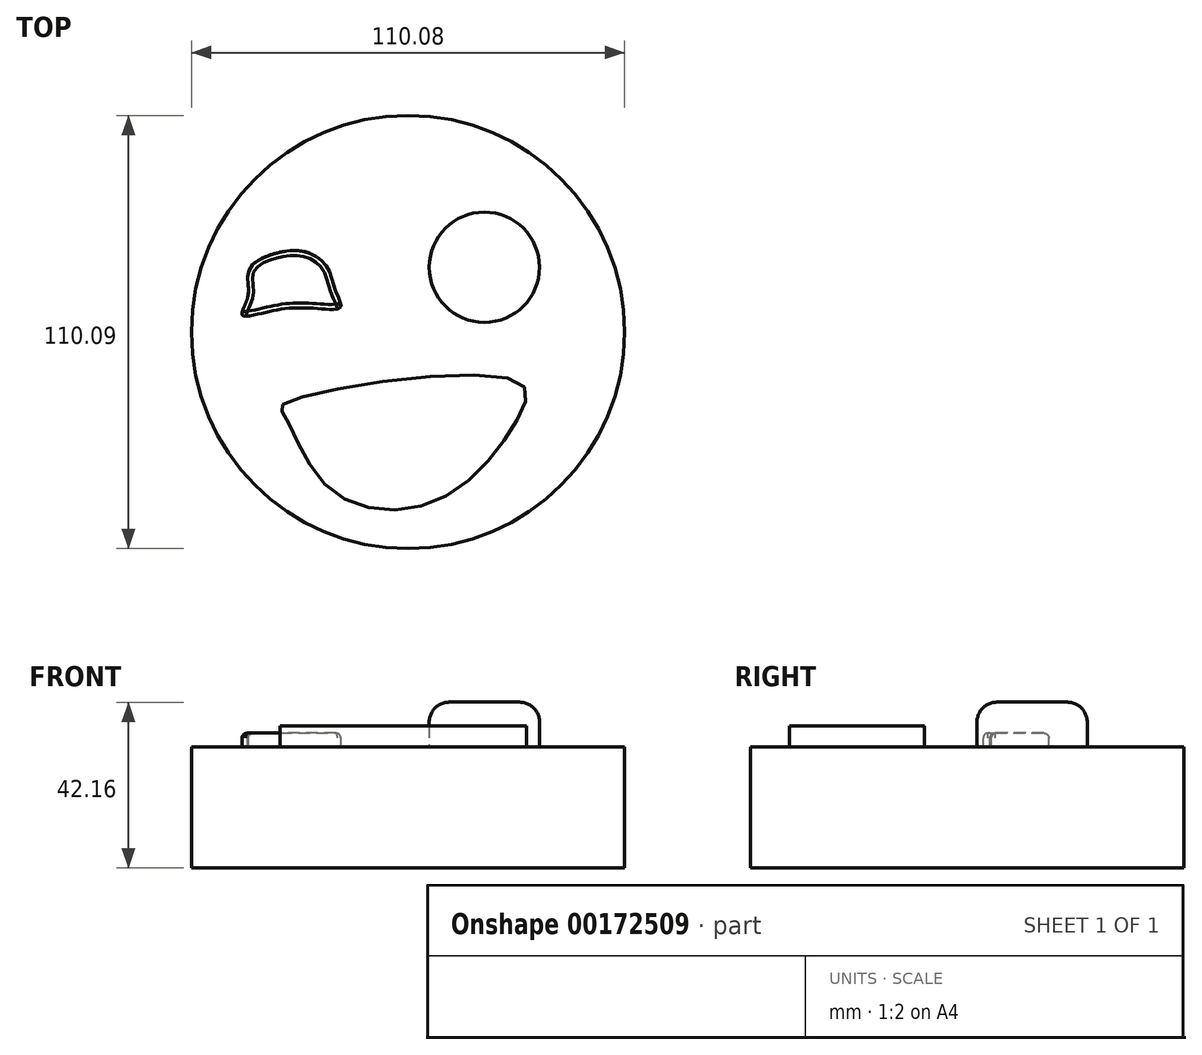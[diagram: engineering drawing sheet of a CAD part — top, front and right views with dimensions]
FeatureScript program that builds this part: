
annotation { "Feature Type Name" : "Feature", "Feature Type Description" : "" }
export const myFeature = defineFeature(function(context is Context, id is Id, definition is map)
    precondition{}
    {
        {
            var Q0;
            Q0=qCreatedBy(makeId("Top.planeOp"),FACE);
            var sketch = newSketch(context, id + "F0", { "sketchPlane" : qUnion([Q0])});
            skCircle(sketch, "E0", {"center": v(0.2, -0.69) * mm, "radius": 55.04 * mm});
            skSolve(sketch);
        }
        {
            var Q0;
            Q0=makeQuery(id+"F0.imprint","IMPRINT",FACE,{"disambiguationData":[TD([[makeQuery(id+"F0.imprint","IMPRINT",EDGE,{"derivedFrom":sQuery(id+"F0.wireOp",EDGE,"E0")}),1.0]])]});
            extrude(context, id + "F1", {"entities" : qUnion([Q0]), "depth" : 30.73 * mm});
        }
        {
            var Q0;
            Q0=makeQuery(id+"F1.opExtrude","CAP_FACE",FACE,{"disambiguationData":[OSD([sQuery(id+"F0.wireOp",EDGE,"E0")])],"isStart":false});
            var sketch = newSketch(context, id + "F2", { "sketchPlane" : qUnion([Q0])});
            skCircle(sketch, "E1", {"center": v(19.59, 15.77) * mm, "radius": 14 * mm});
            skSolve(sketch);
        }
        {
            var Q0;
            Q0=makeQuery(id+"F2.imprint","IMPRINT",FACE,{"disambiguationData":[TD([[makeQuery(id+"F2.imprint","IMPRINT",EDGE,{"derivedFrom":sQuery(id+"F2.wireOp",EDGE,"E1")}),-1.0]])]});
            var sketch = newSketch(context, id + "F3", { "sketchPlane" : qUnion([Q0])});
            skFitSpline(sketch, "E2", {"points": [v(-40.54, 8.13) * mm, v(-40.54, 13.22) * mm, v(-39.17, 16.55) * mm, v(-33.5, 19.3) * mm, v(-25.85, 19.68) * mm, v(-20.37, 15.77) * mm, v(-18.22, 9.7) * mm, v(-17.04, 5.58) * mm, v(-29.77, 5.39) * mm, v(-41.91, 3.62) * mm, v(-40.54, 8.13) * mm]});
            skSolve(sketch);
        }
        {
            var Q0;
            Q0=makeQuery(id+"F2.imprint","IMPRINT",FACE,{"disambiguationData":[TD([[makeQuery(id+"F2.imprint","IMPRINT",EDGE,{"derivedFrom":sQuery(id+"F2.wireOp",EDGE,"E1")}),1.0]])]});
            extrude(context, id + "F4", {"entities" : qUnion([Q0]), "operationType" : NewBodyOperationType.ADD, "depth" : 6.1 * mm});
        }
        {
            var Q0;
            Q0=makeQuery(id+"F3.imprint","IMPRINT",FACE,{"disambiguationData":[TD([[makeQuery(id+"F3.imprint","IMPRINT",EDGE,{"derivedFrom":sQuery(id+"F3.wireOp",EDGE,"E2")}),-1.0]])]});
            extrude(context, id + "F5", {"entities" : qUnion([Q0]), "operationType" : NewBodyOperationType.ADD, "depth" : 3.56 * mm});
        }
        {
            var Q0;
            Q0=makeQuery(id+"F1.opExtrude","CAP_FACE",FACE,{"disambiguationData":[OSD([sQuery(id+"F0.wireOp",EDGE,"E0")])],"isStart":false});
            var sketch = newSketch(context, id + "F6", { "sketchPlane" : qUnion([Q0])});
            skFitSpline(sketch, "E3", {"points": [v(-31.73, -19.1) * mm, v(-31.14, -22.03) * mm, v(-19.78, -40.45) * mm, v(7.25, -43.58) * mm, v(28, -22.82) * mm, v(27.62, -13.02) * mm, v(-31.73, -19.1) * mm]});
            skSolve(sketch);
        }
        {
            var Q0;
            Q0=makeQuery(id+"F6.imprint","IMPRINT",FACE,{"disambiguationData":[TD([[makeQuery(id+"F6.imprint","IMPRINT",EDGE,{"derivedFrom":sQuery(id+"F6.wireOp",EDGE,"E3")}),1.0]])]});
            var Q1;
            Q1=makeQuery(id+"F4.opExtrude","CAP_FACE",FACE,{"disambiguationData":[OSD([sQuery(id+"F2.wireOp",EDGE,"E1")])],"isStart":false});
            extrude(context, id + "F7", {"entities" : qUnion([Q0, Q1]), "operationType" : NewBodyOperationType.ADD, "depth" : 5.33 * mm});
        }
        {
            var Q0;
            Q0=makeQuery(id+"F7.opExtrude","CAP_FACE",FACE,{"disambiguationData":[OSD([sQuery(id+"F2.wireOp",EDGE,"E1")])],"isStart":false});
            fillet(context, id + "F8", {"entities" : qUnion([Q0]), "radius" : 5.08 * mm, "tangentPropagation" : true, "allowEdgeOverflow" : false});
        }
        {
            var Q0;
            Q0=makeQuery(id+"F5.opExtrude","CAP_EDGE",EDGE,{"disambiguationData":[OSD([sQuery(id+"F3.wireOp",EDGE,"E2")])],"isStart":false});
            fillet(context, id + "F9", {"entities" : qUnion([Q0]), "radius" : 1.23 * mm, "tangentPropagation" : true, "allowEdgeOverflow" : false});
        }
    });
